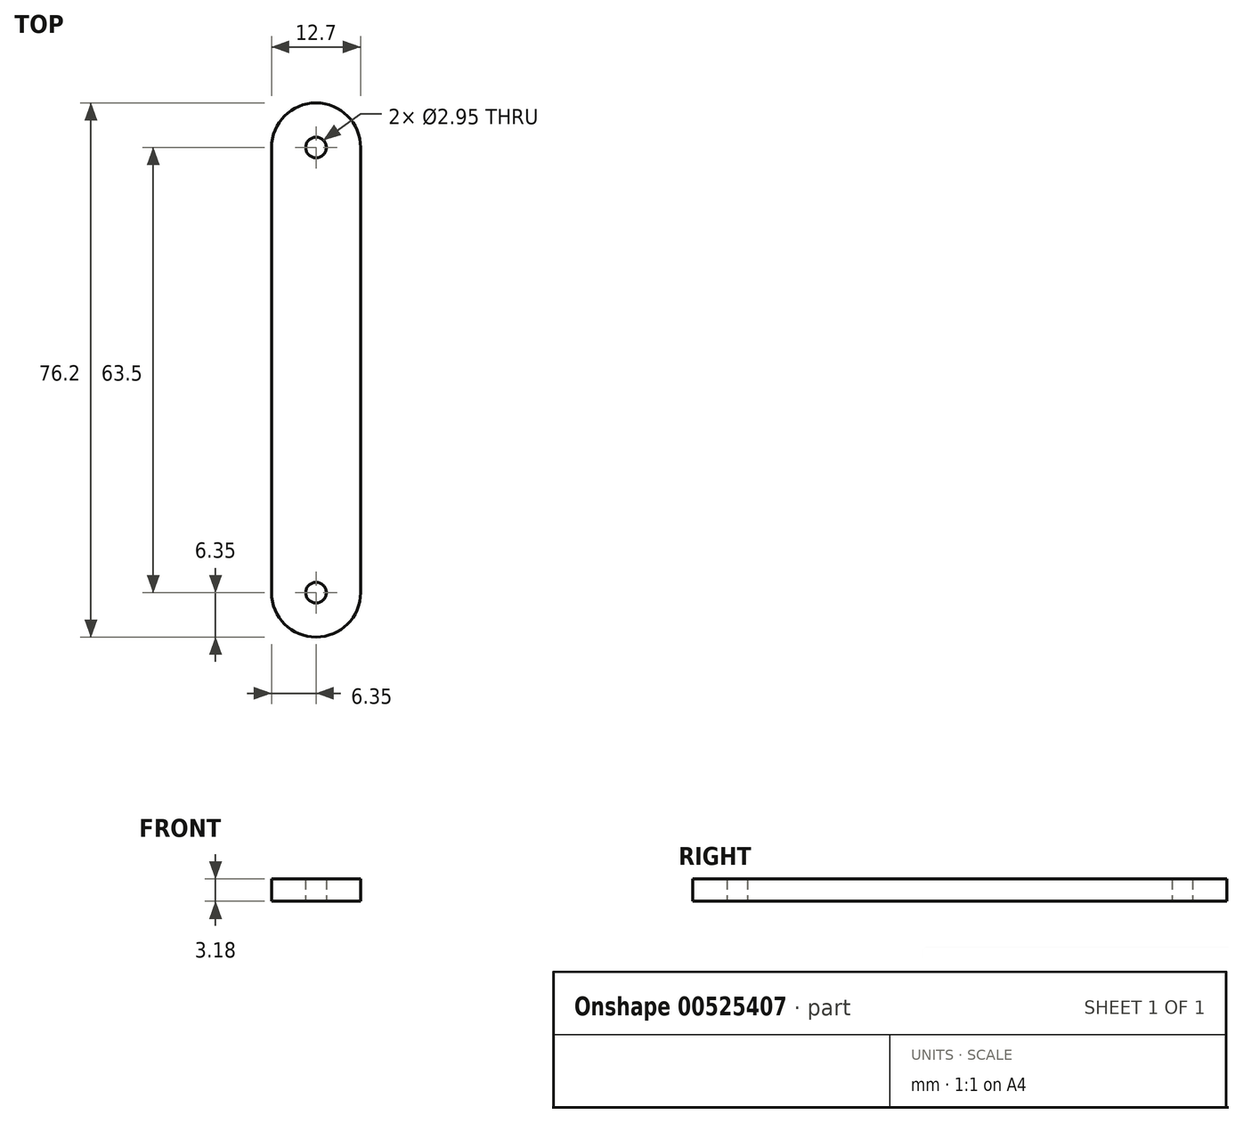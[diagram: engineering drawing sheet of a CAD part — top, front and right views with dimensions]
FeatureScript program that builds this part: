
annotation { "Feature Type Name" : "Feature", "Feature Type Description" : "" }
export const myFeature = defineFeature(function(context is Context, id is Id, definition is map)
    precondition{}
    {
        {
            var Q0;
            Q0=qCreatedBy(makeId("Top.planeOp"),FACE);
            var sketch = newSketch(context, id + "F0", { "sketchPlane" : qUnion([Q0])});
            skLineSegment(sketch, "E0.bottom", {"start": v(0, 38.1) * mm, "end": v(0, 38.1) * mm});
            skLineSegment(sketch, "E0.top", {"start": v(0, -38.1) * mm, "end": v(0, -38.1) * mm});
            skLineSegment(sketch, "E0.left", {"start": v(6.35, 31.75) * mm, "end": v(6.35, -31.75) * mm});
            skLineSegment(sketch, "E0.right", {"start": v(-6.35, 31.75) * mm, "end": v(-6.35, -31.75) * mm});
            skPoint(sketch, "E0.middle", {"position": v(0, 0) * mm});
            skCircle(sketch, "E1", {"center": v(0, -31.75) * mm, "radius": 1.47 * mm});
            skCircle(sketch, "E2.MirrorC", {"center": v(0, 31.75) * mm, "radius": 1.47 * mm});
            skPoint(sketch, "E3.visualSharp", {"position": v(6.35, 38.1) * mm});
            skArc(sketch, "E3.filletArc", {"start": v(6.35, 31.75) * mm, "mid": v(4.5, 36.24) * mm, "end": v(0, 38.1) * mm});
            skPoint(sketch, "E4.visualSharp", {"position": v(-6.35, 38.1) * mm});
            skArc(sketch, "E4.filletArc", {"start": v(0, 38.1) * mm, "mid": v(-4.5, 36.24) * mm, "end": v(-6.35, 31.75) * mm});
            skPoint(sketch, "E5.visualSharp", {"position": v(-6.35, -38.1) * mm});
            skArc(sketch, "E5.filletArc", {"start": v(-6.35, -31.75) * mm, "mid": v(-4.5, -36.24) * mm, "end": v(0, -38.1) * mm});
            skPoint(sketch, "E6.visualSharp", {"position": v(6.35, -38.1) * mm});
            skArc(sketch, "E6.filletArc", {"start": v(0, -38.1) * mm, "mid": v(4.5, -36.24) * mm, "end": v(6.35, -31.75) * mm});
            skSolve(sketch);
        }
        {
            var Q0;
            Q0=makeQuery(id+"F0.imprint","IMPRINT",FACE,{"disambiguationData":[TD([[makeQuery(id+"F0.imprint","IMPRINT",EDGE,{"derivedFrom":sQuery(id+"F0.wireOp",EDGE,"E0.left")}),-1.0]])]});
            extrude(context, id + "F1", {"entities" : qUnion([Q0]), "depth" : 3.17 * mm, "offsetDistance" : 25.4 * mm});
        }
    });
